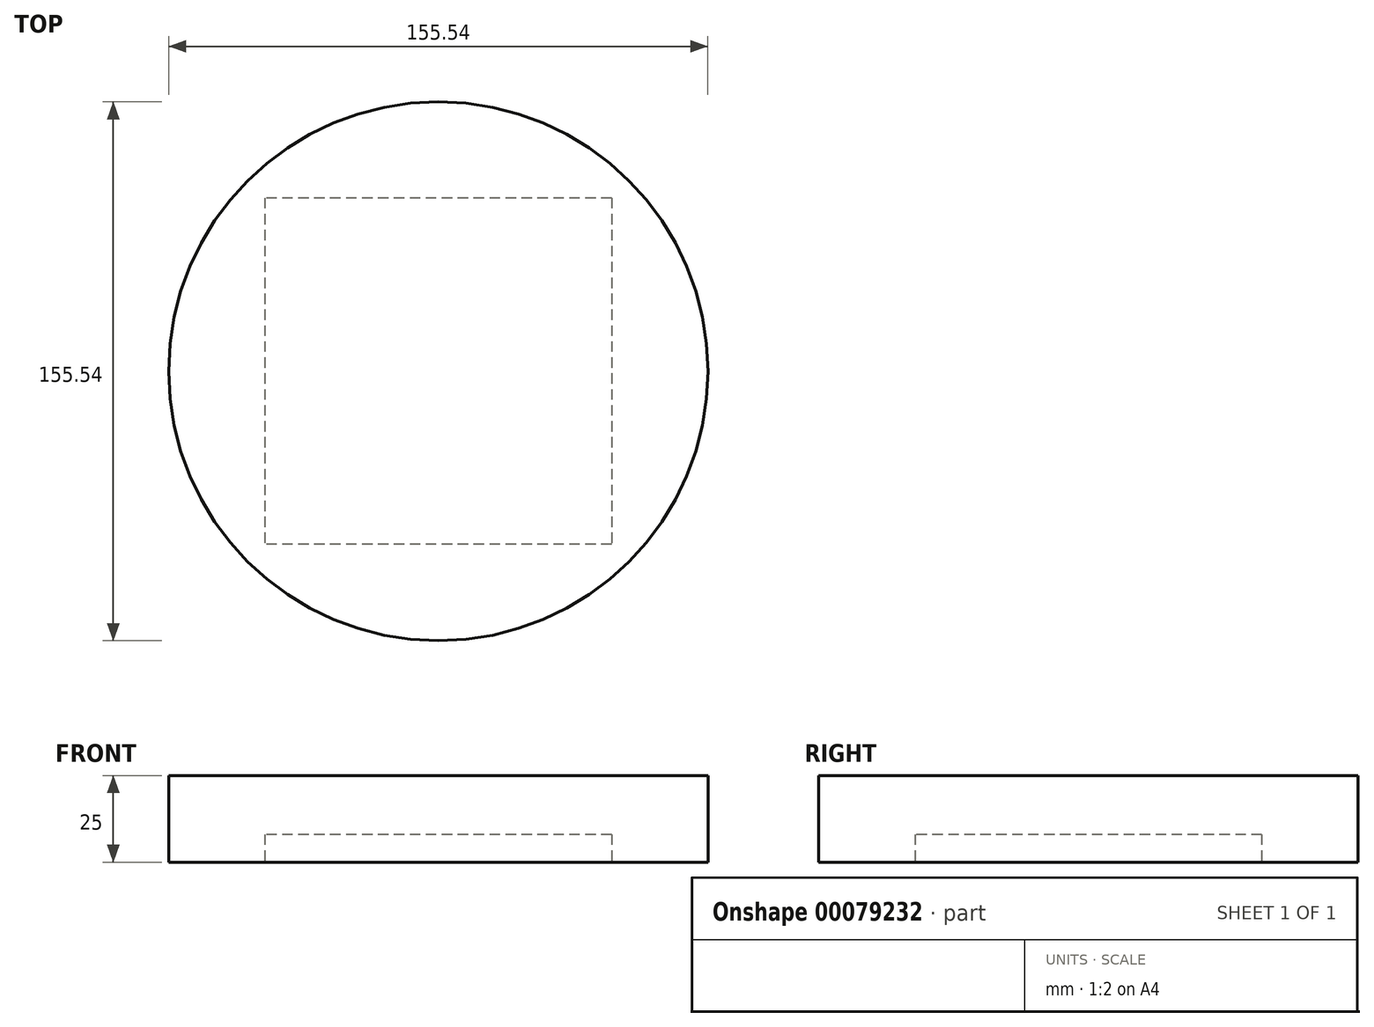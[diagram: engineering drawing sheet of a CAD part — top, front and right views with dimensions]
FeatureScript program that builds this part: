
annotation { "Feature Type Name" : "Feature", "Feature Type Description" : "" }
export const myFeature = defineFeature(function(context is Context, id is Id, definition is map)
    precondition{}
    {
        {
            var Q0;
            Q0=qCreatedBy(makeId("Top.planeOp"),FACE);
            var sketch = newSketch(context, id + "F0", { "sketchPlane" : qUnion([Q0])});
            skLineSegment(sketch, "E0.bottom", {"start": v(50, 50) * mm, "end": v(-50, 50) * mm});
            skLineSegment(sketch, "E0.top", {"start": v(50, -50) * mm, "end": v(-50, -50) * mm});
            skLineSegment(sketch, "E0.left", {"start": v(50, 50) * mm, "end": v(50, -50) * mm});
            skLineSegment(sketch, "E0.right", {"start": v(-50, 50) * mm, "end": v(-50, -50) * mm});
            skPoint(sketch, "E0.middle", {"position": v(0, 0) * mm});
            skCircle(sketch, "E1", {"center": v(0, 0) * mm, "radius": 77.77 * mm});
            skSolve(sketch);
        }
        {
            var Q0;
            Q0=makeQuery(id+"F0.imprint","IMPRINT",FACE,{"disambiguationData":[TD([[makeQuery(id+"F0.imprint","IMPRINT",EDGE,{"derivedFrom":sQuery(id+"F0.wireOp",EDGE,"E0.bottom")}),1.0]])]});
            var Q1;
            Q1=makeQuery(id+"F0.imprint","IMPRINT",FACE,{"disambiguationData":[TD([[makeQuery(id+"F0.imprint","IMPRINT",EDGE,{"derivedFrom":sQuery(id+"F0.wireOp",EDGE,"E0.bottom")}),-1.0]])]});
            extrude(context, id + "F1", {"entities" : qUnion([Q0, Q1]), "depth" : 25 * mm});
        }
        {
            var Q0;
            Q0=makeQuery(id+"F0.imprint","IMPRINT",FACE,{"disambiguationData":[TD([[makeQuery(id+"F0.imprint","IMPRINT",EDGE,{"derivedFrom":sQuery(id+"F0.wireOp",EDGE,"E0.bottom")}),1.0]])]});
            extrude(context, id + "F2", {"entities" : qUnion([Q0]), "operationType" : NewBodyOperationType.REMOVE, "depth" : 8 * mm});
        }
    });
